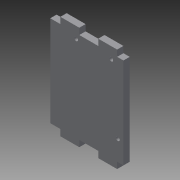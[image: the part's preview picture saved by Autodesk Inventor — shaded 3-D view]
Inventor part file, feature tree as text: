
AUTODESK INVENTOR PART (.ipt)
format: ipt  version: 2014 (Build 180170000, 170)  size: 105,472 bytes
history: native  units: mm
features: reference x5, extrude x1, sketch x1
ambient origin geometry x8: Origin, YZ Plane, XZ Plane, XY Plane, X Axis, Y Axis, Z Axis, Center Point
bodies: 实体1 (feature_tree)
feature tree (7):
  extrude  "拉伸1"  Depth=5.0mm
  sketch  "草图2"  dims[d1=53.3mm d2=68.6mm d3=2.0mm d4=2.0mm d5=5.0mm d6=3.0mm d7=14.0mm d8=2.5mm d9=3.0mm d10=5.1mm d11=52.1mm d12=3.0mm d13=27.9mm d14=5.0mm d15=5.0mm d16=0.0mm]
  reference  "参考1"
  reference  "参考2"
  reference  "参考3"
  reference  "参考4"
  reference  "参考5"
